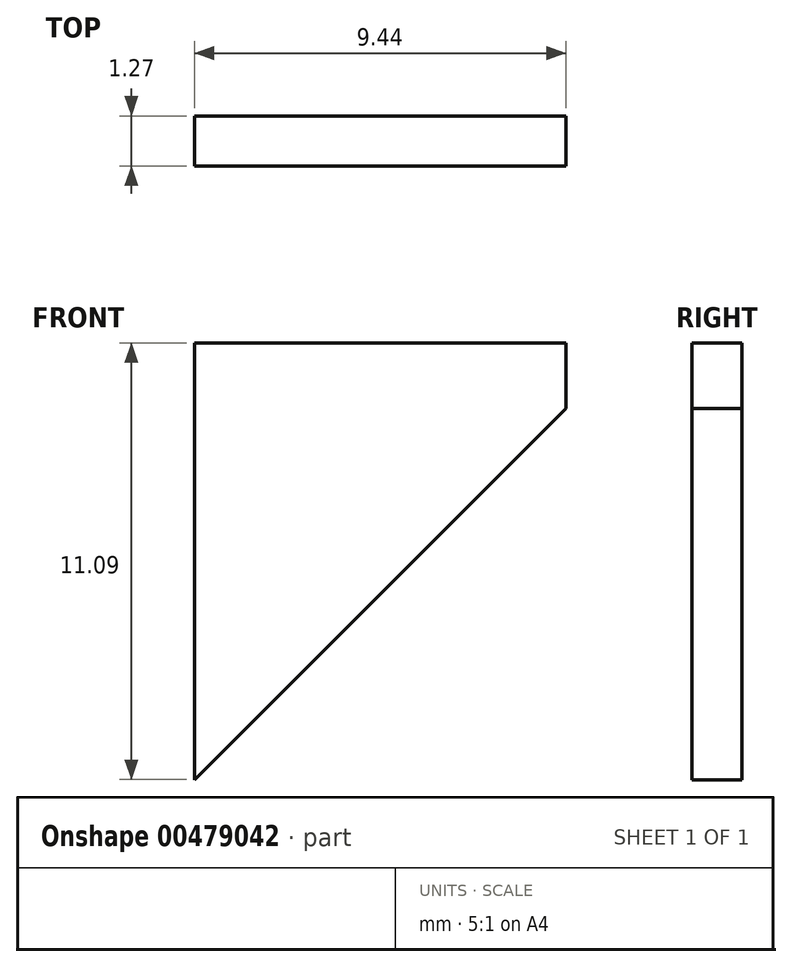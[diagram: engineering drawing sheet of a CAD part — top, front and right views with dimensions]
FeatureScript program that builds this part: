
annotation { "Feature Type Name" : "Feature", "Feature Type Description" : "" }
export const myFeature = defineFeature(function(context is Context, id is Id, definition is map)
    precondition{}
    {
        {
            var Q0;
            Q0=qCreatedBy(makeId("Front.planeOp"),FACE);
            var sketch = newSketch(context, id + "F0", { "sketchPlane" : qUnion([Q0])});
            skLineSegment(sketch, "E0.bottom", {"start": v(-39.24, 42.26) * mm, "end": v(-29.8, 42.26) * mm});
            skLineSegment(sketch, "E0.top", {"start": v(-39.24, 30.44) * mm, "end": v(-29.8, 30.44) * mm});
            skLineSegment(sketch, "E0.left", {"start": v(-39.24, 42.26) * mm, "end": v(-39.24, 30.44) * mm});
            skLineSegment(sketch, "E0.right", {"start": v(-29.8, 42.26) * mm, "end": v(-29.8, 30.44) * mm});
            skSolve(sketch);
        }
        {
            var Q0;
            Q0=makeQuery(id+"F0.imprint","IMPRINT",FACE,{"disambiguationData":[TD([[makeQuery(id+"F0.imprint","IMPRINT",EDGE,{"derivedFrom":sQuery(id+"F0.wireOp",EDGE,"E0.bottom")}),-1.0]])]});
            extrude(context, id + "F1", {"entities" : qUnion([Q0]), "depth" : 1.27 * mm});
        }
        {
            var Q0;
            Q0=makeQuery(id+"F1.opExtrude","SWEPT_EDGE",EDGE,{"disambiguationData":[OSD([sQuery(id+"F0.wireOp",EDGE,"E0.top"),sQuery(id+"F0.wireOp",EDGE,"E0.right")])]});
            chamfer(context, id + "F2", {"entities" : qUnion([Q0]), "width" : 10.16 * mm, "tangentPropagation" : true});
        }
    });
